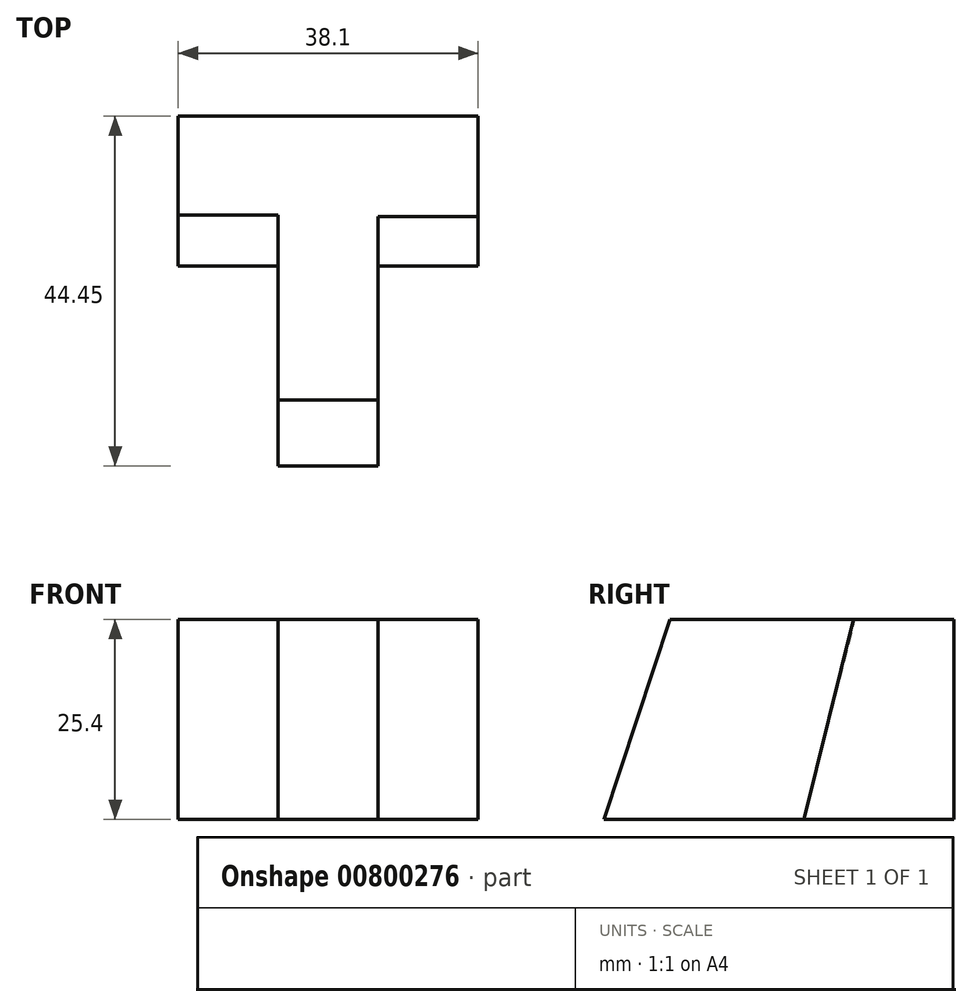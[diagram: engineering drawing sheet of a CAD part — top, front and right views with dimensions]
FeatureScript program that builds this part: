
annotation { "Feature Type Name" : "Feature", "Feature Type Description" : "" }
export const myFeature = defineFeature(function(context is Context, id is Id, definition is map)
    precondition{}
    {
        {
            var Q0;
            Q0=qCreatedBy(makeId("Top.planeOp"),FACE);
            var sketch = newSketch(context, id + "F0", { "sketchPlane" : qUnion([Q0])});
            skLineSegment(sketch, "E0", {"start": v(0, 0) * mm, "end": v(12.7, 0) * mm});
            skLineSegment(sketch, "E1", {"start": v(12.7, 0) * mm, "end": v(12.7, 25.4) * mm});
            skLineSegment(sketch, "E2", {"start": v(12.7, 25.4) * mm, "end": v(25.4, 25.4) * mm});
            skLineSegment(sketch, "E3", {"start": v(25.4, 25.4) * mm, "end": v(25.4, 44.45) * mm});
            skLineSegment(sketch, "E4", {"start": v(25.4, 44.45) * mm, "end": v(-12.7, 44.45) * mm});
            skLineSegment(sketch, "E5", {"start": v(-12.7, 44.45) * mm, "end": v(-12.7, 25.4) * mm});
            skLineSegment(sketch, "E6", {"start": v(-12.7, 25.4) * mm, "end": v(0, 25.4) * mm});
            skLineSegment(sketch, "E7", {"start": v(0, 25.4) * mm, "end": v(0, 0) * mm});
            skSolve(sketch);
        }
        {
            var Q0;
            Q0=makeQuery(id+"F0.imprint","IMPRINT",FACE,{"disambiguationData":[TD([[makeQuery(id+"F0.imprint","IMPRINT",EDGE,{"derivedFrom":sQuery(id+"F0.wireOp",EDGE,"E0")}),1.0]])]});
            extrude(context, id + "F1", {"entities" : qUnion([Q0]), "depth" : 25.4 * mm});
        }
        {
            var Q0;
            Q0=makeQuery(id+"F1.opExtrude","SWEPT_FACE",FACE,{"disambiguationData":[OSD([sQuery(id+"F0.wireOp",EDGE,"E7")])]});
            var sketch = newSketch(context, id + "F2", { "sketchPlane" : qUnion([Q0])});
            skLineSegment(sketch, "E8", {"start": v(0, 0) * mm, "end": v(-8.36, 25.4) * mm});
            skSolve(sketch);
        }
        {
            var Q0;
            Q0=qSketchRegion(id+"F2",true);
            var Q1;
            {var subQ0=sQuery(id+"F2.wireOp",EDGE,"E8");Q1=makeQuery(id+"F2.imprint","IMPRINT",FACE,{"disambiguationData":[TD([[makeQuery(id+"F2.imprint","IMPRINT",EDGE,{"derivedFrom":subQ0}),-1.0]])]});}
            extrude(context, id + "F3", {"entities" : qUnion([Q0, Q1]), "operationType" : NewBodyOperationType.REMOVE, "oppositeDirection" : true, "depth" : 25.4 * mm});
        }
        {
            var Q0;
            Q0=makeQuery(id+"F1.opExtrude","SWEPT_FACE",FACE,{"disambiguationData":[OSD([sQuery(id+"F0.wireOp",EDGE,"E5")])]});
            var sketch = newSketch(context, id + "F4", { "sketchPlane" : qUnion([Q0])});
            skLineSegment(sketch, "E9", {"start": v(-25.4, 0) * mm, "end": v(-31.88, 25.4) * mm});
            skSolve(sketch);
        }
        {
            var Q0;
            Q0=makeQuery(id+"F1.opExtrude","SWEPT_FACE",FACE,{"disambiguationData":[OSD([sQuery(id+"F0.wireOp",EDGE,"E3")])]});
            var sketch = newSketch(context, id + "F5", { "sketchPlane" : qUnion([Q0])});
            skLineSegment(sketch, "E10", {"start": v(31.67, 25.4) * mm, "end": v(25.4, 0) * mm});
            skSolve(sketch);
        }
        {
            var Q0;
            Q0=qSketchRegion(id+"F5",true);
            var Q1;
            {var subQ0=sQuery(id+"F5.wireOp",EDGE,"E10");Q1=makeQuery(id+"F5.imprint","IMPRINT",FACE,{"disambiguationData":[TD([[makeQuery(id+"F5.imprint","IMPRINT",EDGE,{"derivedFrom":subQ0}),-1.0]])]});}
            extrude(context, id + "F6", {"entities" : qUnion([Q0, Q1]), "operationType" : NewBodyOperationType.REMOVE, "oppositeDirection" : true, "depth" : 12.7 * mm});
        }
        {
            var Q0;
            {var subQ0=sQuery(id+"F4.wireOp",EDGE,"E9");Q0=makeQuery(id+"F4.imprint","IMPRINT",FACE,{"disambiguationData":[TD([[makeQuery(id+"F4.imprint","IMPRINT",EDGE,{"derivedFrom":subQ0}),-1.0]])]});}
            extrude(context, id + "F7", {"entities" : qUnion([Q0]), "operationType" : NewBodyOperationType.REMOVE, "oppositeDirection" : true, "depth" : 12.7 * mm});
        }
    });
